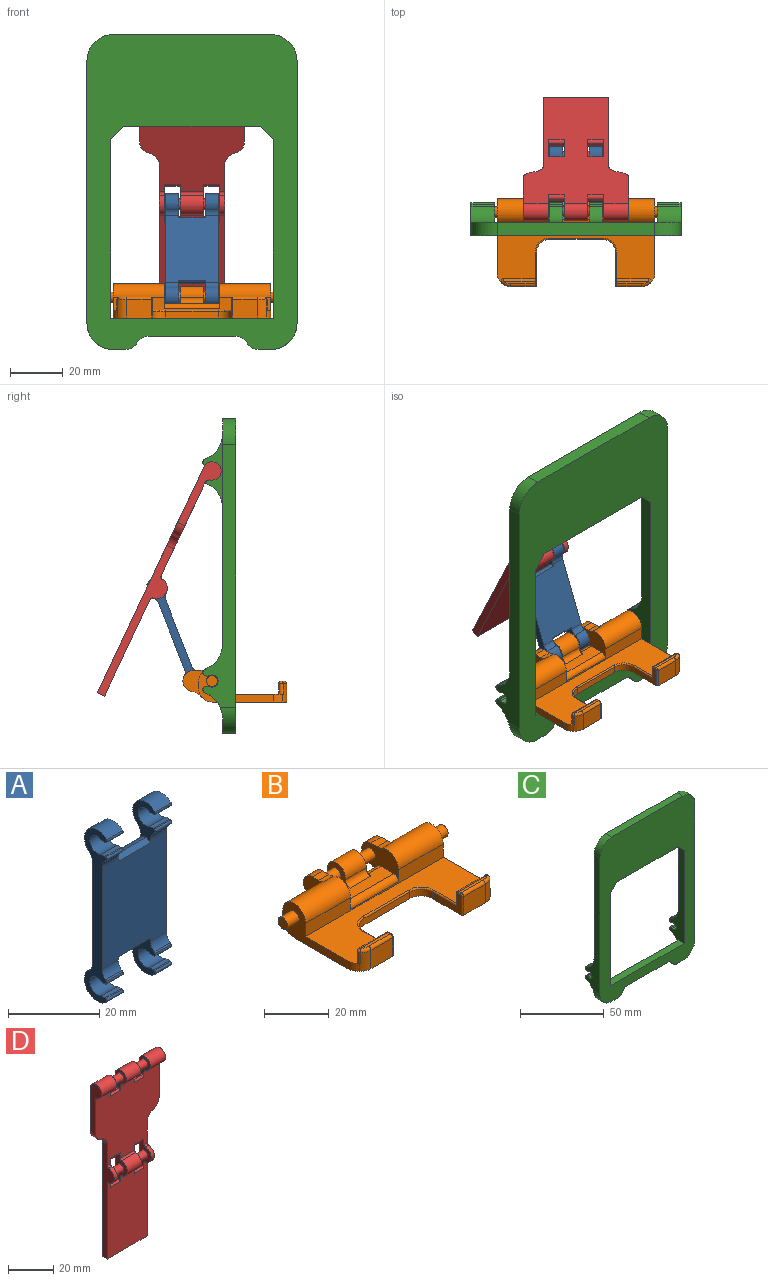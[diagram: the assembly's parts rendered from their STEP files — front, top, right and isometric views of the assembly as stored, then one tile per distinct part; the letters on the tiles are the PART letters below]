
ASSEMBLY  parts=4 mates=4
PART A: 56 faces, bbox 20x7x46 mm
  f0: cylinder r=3mm len=5mm, axis (-1,0,0), area 13.1mm2, adj f4,f7,f13,f17
  f1: cylinder r=3mm len=5mm, axis (-1,0,0), area 13.1mm2, adj f5,f7,f11,f16
  f2: cylinder r=3mm len=5mm, axis (-1,0,0), area 13.1mm2, adj f6,f10,f17,f19
  f3: cylinder r=3mm len=5mm, axis (-1,0,0), area 13.1mm2, adj f6,f12,f16,f18
  f4: cylinder r=4mm len=7.06mm, axis (-1,0,0), area 65mm2, adj f0,f7,f13,f41
  f5: cylinder r=4mm len=5mm, axis (-1,0,0), area 2.1mm2, adj f1,f7,f11,f44
  f6: plane 46x7.02mm, normal (1,0,0), area 144.3mm2, adj f2,f3,f8,f9,f16,f17,f18,f19
  f7: plane 46x7.02mm, normal (-1,0,0), area 144.3mm2, adj f0,f1,f4,f5,f14,f15,f16,f17
  f8: cylinder r=4mm len=7.06mm, axis (-1,0,0), area 65mm2, adj f6,f12,f42,f48
  f9: cylinder r=4mm len=5mm, axis (-1,0,0), area 2.1mm2, adj f6,f10,f46,f49
  f10: plane 10.2x7.02mm, normal (-1,0,0), area 32.3mm2, adj f2,f9,f16,f17,f19,f29,f30,f31
  f11: plane 10.2x7.02mm, normal (1,0,0), area 32.3mm2, adj f1,f5,f15,f16,f17,f26,f27,f28
  f12: plane 10.2x7.02mm, normal (-1,0,0), area 32.3mm2, adj f3,f8,f16,f17,f18,f23,f24,f25
  f13: plane 10.2x7.02mm, normal (1,0,0), area 32.3mm2, adj f0,f4,f14,f16,f17,f20,f21,f22
  f14: cylinder r=4mm len=5mm, axis (-1,0,0), area 2.1mm2, adj f7,f13,f40,f51
  f15: cylinder r=4mm len=7.06mm, axis (-1,0,0), area 65mm2, adj f7,f11,f45,f50
  f16: plane 27.28x20mm, normal (0,-1,0), area 528.8mm2, adj f1,f3,f6,f7,f10,f11,f12,f13
  f17: plane 27.28x20mm, normal (0,1,0), area 528.8mm2, adj f0,f2,f6,f7,f10,f11,f12,f13
  f18: cylinder r=4mm len=5mm, axis (-1,0,0), area 2.1mm2, adj f3,f6,f12,f43
  f19: cylinder r=4mm len=7.06mm, axis (-1,0,0), area 65mm2, adj f2,f6,f10,f47
  f20: plane 5x1.07mm, normal (0,0,1), area 5.4mm2, adj f7,f13,f22,f32
  f21: plane 5x1.07mm, normal (0,0,-1), area 5.4mm2, adj f7,f13,f22,f33
  f22: cylinder r=2.3mm len=5mm, axis (-1,0,0), area 49.9mm2, adj f7,f13,f20,f21
  f23: cylinder r=2.3mm len=5mm, axis (-1,0,0), area 49.9mm2, adj f6,f12,f24,f25
  f24: plane 5x1.07mm, normal (0,0,-1), area 5.4mm2, adj f6,f12,f23,f34
  f25: plane 5x1.07mm, normal (0,0,1), area 5.4mm2, adj f6,f12,f23,f35
  f26: plane 5x1.07mm, normal (0,0,1), area 5.4mm2, adj f7,f11,f28,f37
  f27: plane 5x1.07mm, normal (0,0,-1), area 5.4mm2, adj f7,f11,f28,f36
  f28: cylinder r=2.3mm len=5mm, axis (-1,0,0), area 49.9mm2, adj f7,f11,f26,f27
  f29: cylinder r=2.3mm len=5mm, axis (-1,0,0), area 49.9mm2, adj f6,f10,f30,f31
  f30: plane 5x1.07mm, normal (0,0,-1), area 5.4mm2, adj f6,f10,f29,f38
  f31: plane 5x1.07mm, normal (0,0,1), area 5.4mm2, adj f6,f10,f29,f39
  f32: cylinder r=1mm len=5mm, axis (-1,0,0), area 1.6mm2, adj f7,f13,f20,f40
  f33: cylinder r=1mm len=5mm, axis (-1,0,0), area 1.6mm2, adj f7,f13,f21,f41
  f34: cylinder r=1mm len=5mm, axis (-1,0,0), area 1.6mm2, adj f6,f12,f24,f42
  f35: cylinder r=1mm len=5mm, axis (-1,0,0), area 1.6mm2, adj f6,f12,f25,f43
  f36: cylinder r=1mm len=5mm, axis (-1,0,0), area 1.6mm2, adj f7,f11,f27,f44
  f37: cylinder r=1mm len=5mm, axis (-1,0,0), area 1.6mm2, adj f7,f11,f26,f45
  f38: cylinder r=1mm len=5mm, axis (-1,0,0), area 1.6mm2, adj f6,f10,f30,f46
  f39: cylinder r=1mm len=5mm, axis (-1,0,0), area 1.6mm2, adj f6,f10,f31,f47
  f40: cylinder r=0.5mm len=5mm, axis (-1,0,0), area 5mm2, adj f7,f13,f14,f32
  f41: cylinder r=0.5mm len=5mm, axis (1,0,0), area 5mm2, adj f4,f7,f13,f33
  f42: cylinder r=0.5mm len=5mm, axis (1,0,0), area 5mm2, adj f6,f8,f12,f34
  f43: cylinder r=0.5mm len=5mm, axis (-1,0,0), area 5mm2, adj f6,f12,f18,f35
  f44: cylinder r=0.5mm len=5mm, axis (1,0,0), area 5mm2, adj f5,f7,f11,f36
  f45: cylinder r=0.5mm len=5mm, axis (-1,0,0), area 5mm2, adj f7,f11,f15,f37
  f46: cylinder r=0.5mm len=5mm, axis (1,0,0), area 5mm2, adj f6,f9,f10,f38
  f47: cylinder r=0.5mm len=5mm, axis (-1,0,0), area 5mm2, adj f6,f10,f19,f39
  f48: cylinder r=3mm len=5mm, axis (-1,0,0), area 13.1mm2, adj f6,f8,f12,f17
  f49: cylinder r=3mm len=5mm, axis (-1,0,0), area 13.1mm2, adj f6,f9,f10,f16
  f50: cylinder r=3mm len=5mm, axis (-1,0,0), area 13.1mm2, adj f7,f11,f15,f17
  f51: cylinder r=3mm len=5mm, axis (-1,0,0), area 13.1mm2, adj f7,f13,f14,f16
  f52: cylinder r=2mm len=10mm, axis (-1,0,0), area 17.1mm2, adj f12,f13,f17,f53
  f53: cylinder r=2mm len=10mm, axis (1,0,0), area 17.1mm2, adj f12,f13,f16,f52
  f54: cylinder r=2mm len=10mm, axis (-1,0,0), area 17.1mm2, adj f10,f11,f16,f55
  f55: cylinder r=2mm len=10mm, axis (1,0,0), area 17.1mm2, adj f10,f11,f17,f54
PART B: 79 faces, bbox 70x39.9x13 mm
  f0: plane 60x22.15mm, normal (0,0,1), area 757.9mm2, adj f8,f9,f10,f43,f44,f46,f48,f50
  f1: plane 9.43x7mm, normal (0,-1,0), area 66mm2, adj f5,f50,f63,f78
  f2: cylinder r=2mm len=6mm, axis (-1,0,0), area 75.4mm2, adj f19,f28
  f3: cylinder r=5mm len=19.5mm, axis (-1,0,0), area 281.1mm2, adj f4,f8,f10,f14,f15,f42
  f4: plane 15x3mm, normal (0,1,0), area 45mm2, adj f3,f8,f14,f20
  f5: plane 60x28.4mm, normal (0,0,-1), area 1163.5mm2, adj f1,f7,f8,f9,f20,f34,f35,f36
  f6: plane 15x3mm, normal (0,1,0), area 45mm2, adj f9,f11,f18,f20
  f7: plane 9.43x7mm, normal (0,-1,0), area 66mm2, adj f5,f53,f59,f64
  f8: plane 28.33x13mm, normal (1,0,0), area 155mm2, adj f0,f3,f4,f5,f10,f20,f23,f52
  f9: plane 28.33x13mm, normal (-1,0,0), area 155mm2, adj f0,f5,f6,f10,f11,f20,f25,f51
  f10: plane 60x5mm, normal (0,-1,0), area 205.5mm2, adj f0,f3,f8,f9,f11,f15,f19,f45
  f11: cylinder r=5mm len=19.5mm, axis (-1,0,0), area 281.1mm2, adj f6,f9,f10,f18,f19,f41
  f12: plane 4.5x2.74mm, normal (0,0,1), area 12.3mm2, adj f13,f14,f15,f42
  f13: cylinder r=4mm len=7.96mm, axis (-1,0,0), area 53.9mm2, adj f12,f14,f15,f33
  f14: plane 10.63x8.92mm, normal (1,0,0), area 46mm2, adj f3,f4,f12,f13,f20,f33,f42
  f15: plane 16.1x11.13mm, normal (-1,0,0), area 100.1mm2, adj f3,f10,f12,f13,f20,f21,f26,f33
  f16: plane 4.5x2.74mm, normal (0,0,1), area 12.3mm2, adj f17,f18,f19,f41
  f17: cylinder r=4mm len=7.96mm, axis (1,0,0), area 53.9mm2, adj f16,f18,f19,f32
  f18: plane 10.63x8.92mm, normal (-1,0,0), area 46mm2, adj f6,f11,f16,f17,f20,f32,f41
  f19: plane 16.1x11.13mm, normal (1,0,0), area 100.1mm2, adj f2,f10,f11,f16,f17,f20,f21,f32
  f20: cylinder r=5mm len=60mm, axis (1,0,0), area 378.9mm2, adj f4,f5,f6,f8,f9,f14,f15,f18
  f21: plane 21x5.6mm, normal (0,0,1), area 104.3mm2, adj f15,f19,f27,f28,f30,f39,f40,f45
  f22: plane 4.2x4.2mm, normal (1,0,0), area 13.9mm2, adj f23
  f23: cylinder r=2.1mm len=5mm, axis (-1,0,0), area 66mm2, adj f8,f22
  f24: plane 4.2x4.2mm, normal (-1,0,0), area 13.9mm2, adj f25
  f25: cylinder r=2.1mm len=5mm, axis (1,0,0), area 66mm2, adj f9,f24
  f26: cylinder r=2mm len=6mm, axis (-1,0,0), area 75.4mm2, adj f15,f27
  f27: plane 10.13x9.98mm, normal (1,0,0), area 42.2mm2, adj f20,f21,f26,f29,f30,f31,f40
  f28: plane 10.13x9.98mm, normal (-1,0,0), area 42.2mm2, adj f2,f20,f21,f29,f30,f31,f39
  f29: cylinder r=4mm len=9mm, axis (-1,0,0), area 167.3mm2, adj f27,f28,f30,f31
  f30: cylinder r=2mm len=9mm, axis (-1,0,0), area 29.8mm2, adj f21,f27,f28,f29
  f31: cylinder r=6mm len=9mm, axis (-1,0,0), area 40.3mm2, adj f20,f27,f28,f29
  f32: cylinder r=6mm len=4.5mm, axis (1,0,0), area 20.1mm2, adj f17,f18,f19,f20
  f33: cylinder r=6mm len=4.5mm, axis (1,0,0), area 20.1mm2, adj f13,f14,f15,f20
  f34: plane 20x2.5mm, normal (0,-1,0), area 50mm2, adj f5,f37,f38,f71
  f35: plane 12.5x7.5mm, normal (1,0,0), area 41.1mm2, adj f5,f37,f73,f74,f75,f76,f77,f78
  f36: plane 12.5x7.5mm, normal (-1,0,0), area 41.1mm2, adj f5,f38,f64,f65,f66,f67,f68,f69
  f37: cylinder r=5mm len=5mm, axis (0,0,1), area 19.6mm2, adj f5,f34,f35,f72
  f38: cylinder r=5mm len=5mm, axis (0,0,-1), area 19.6mm2, adj f5,f34,f36,f70
  f39: cylinder r=2mm len=6mm, axis (1,0,0), area 25.1mm2, adj f19,f20,f21,f28
  f40: cylinder r=2mm len=6mm, axis (1,0,0), area 25.1mm2, adj f15,f20,f21,f27
  f41: cylinder r=5mm len=4.5mm, axis (-1,0,0), area 10.1mm2, adj f11,f16,f18,f19
  f42: cylinder r=5mm len=4.5mm, axis (-1,0,0), area 10.1mm2, adj f3,f12,f14,f15
  f43: plane 3x0.07mm, normal (0.71,-0.71,0), area 0.3mm2, adj f0,f5,f52,f53
  f44: plane 3x0.07mm, normal (-0.71,-0.71,0), area 0.3mm2, adj f0,f5,f50,f51
  f45: cylinder r=2mm len=21mm, axis (-1,0,0), area 66mm2, adj f10,f15,f19,f21
  f46: plane 12.07x4mm, normal (0,1,0), area 48.3mm2, adj f0,f55,f60,f74
  f47: plane 12.07x1mm, normal (0,0,1), area 11.2mm2, adj f55,f62,f63,f76
  f48: plane 12.07x4mm, normal (0,1,0), area 48.3mm2, adj f0,f54,f56,f68
  f49: plane 12.07x1mm, normal (0,0,1), area 11.2mm2, adj f54,f58,f59,f66
  f50: cylinder r=5mm len=7mm, axis (0,0,-1), area 26.2mm2, adj f0,f1,f5,f44,f60,f62
  f51: cylinder r=5mm len=3.54mm, axis (0,0,-1), area 11.8mm2, adj f0,f5,f9,f44
  f52: cylinder r=5mm len=3.54mm, axis (0,0,1), area 11.8mm2, adj f0,f5,f8,f43
  f53: cylinder r=5mm len=7mm, axis (0,0,-1), area 26.2mm2, adj f0,f5,f7,f43,f56,f58
  f54: cylinder r=1mm len=12.07mm, axis (1,0,0), area 19mm2, adj f48,f49,f57,f67
  f55: cylinder r=1mm len=12.07mm, axis (1,0,0), area 19mm2, adj f46,f47,f61,f75
  f56: cylinder r=1mm len=4mm, axis (0,0,-1), area 9.7mm2, adj f0,f48,f53,f57
  f57: sphere r=1mm, area 2.4mm2, adj f54,f56,f58
  f58: torus R=4mm, axis (0,0,1), area 5.3mm2, adj f49,f53,f57,f59
  f59: cylinder r=1mm len=9.43mm, axis (-1,0,0), area 14.8mm2, adj f7,f49,f58,f65
  f60: cylinder r=1mm len=4mm, axis (0,0,-1), area 9.7mm2, adj f0,f46,f50,f61
  f61: sphere r=1mm, area 2.4mm2, adj f55,f60,f62
  f62: torus R=4mm, axis (0,0,1), area 5.3mm2, adj f47,f50,f61,f63
  f63: cylinder r=1mm len=9.43mm, axis (-1,0,0), area 14.8mm2, adj f1,f47,f62,f77
  f64: cylinder r=0.5mm len=7mm, axis (0,0,1), area 5.5mm2, adj f5,f7,f36,f65
  f65: torus R=0.5mm, axis (-1,0,0), area 1mm2, adj f36,f59,f64,f66
  f66: cylinder r=0.5mm len=1mm, axis (0,-1,0), area 0.8mm2, adj f36,f49,f65,f67
  f67: torus R=0.5mm, axis (-1,0,0), area 1mm2, adj f36,f54,f66,f68
  f68: cylinder r=0.5mm len=4.5mm, axis (0,0,-1), area 3.3mm2, adj f36,f48,f67,f69
  f69: cylinder r=0.5mm len=10.5mm, axis (0,1,0), area 8mm2, adj f0,f36,f68,f70
  f70: torus R=5.5mm, axis (0,0,-1), area 6.4mm2, adj f0,f38,f69,f71
  f71: cylinder r=0.5mm len=20mm, axis (-1,0,0), area 15.7mm2, adj f0,f34,f70,f72
  f72: torus R=5.5mm, axis (0,0,-1), area 6.4mm2, adj f0,f37,f71,f73
  f73: cylinder r=0.5mm len=10.5mm, axis (0,-1,0), area 8mm2, adj f0,f35,f72,f74
  f74: cylinder r=0.5mm len=4.5mm, axis (0,0,-1), area 3.3mm2, adj f35,f46,f73,f75
  f75: torus R=0.5mm, axis (-1,0,0), area 1mm2, adj f35,f55,f74,f76
  f76: cylinder r=0.5mm len=1mm, axis (0,1,0), area 0.8mm2, adj f35,f47,f75,f77
  f77: torus R=0.5mm, axis (-1,0,0), area 1mm2, adj f35,f63,f76,f78
  f78: cylinder r=0.5mm len=7mm, axis (0,0,-1), area 5.5mm2, adj f1,f5,f35,f77
PART C: 79 faces, bbox 80x12.5x120 mm
  f0: plane 78.31x11.9mm, normal (0,1,0), area 594.8mm2, adj f3,f6,f9,f10,f12,f13,f14,f15
  f1: plane 120x80mm, normal (0,-1,0), area 4797.1mm2, adj f3,f4,f5,f6,f7,f8,f9,f10
  f2: plane 85.98x80mm, normal (0,1,0), area 3419.3mm2, adj f4,f5,f7,f8,f11,f17,f18,f24
  f3: plane 5x4.68mm, normal (0,0,-1), area 23.4mm2, adj f0,f1,f9,f16
  f4: plane 60x5mm, normal (0,0,1), area 300mm2, adj f1,f2,f8,f11
  f5: plane 100x12.49mm, normal (-1,0,0), area 577.9mm2, adj f1,f2,f8,f9,f38,f39,f40,f41
  f6: plane 5x4.68mm, normal (0,0,-1), area 23.4mm2, adj f0,f1,f10,f15
  f7: plane 100x12.49mm, normal (1,0,0), area 577.9mm2, adj f1,f2,f10,f11,f25,f26,f27,f28
  f8: cylinder r=10mm len=10mm, axis (0,1,0), area 78.5mm2, adj f1,f2,f4,f5
  f9: cylinder r=10mm len=10mm, axis (0,-1,0), area 79.7mm2, adj f0,f1,f3,f5,f60
  f10: cylinder r=10mm len=10mm, axis (0,1,0), area 79.7mm2, adj f0,f1,f6,f7,f63
  f11: cylinder r=10mm len=10mm, axis (0,-1,0), area 78.5mm2, adj f1,f2,f4,f7
  f12: plane 33.32x5mm, normal (0,0,-1), area 166.6mm2, adj f0,f1,f13,f14
  f13: cylinder r=5mm len=5mm, axis (0,1,0), area 26.2mm2, adj f0,f1,f12,f16
  f14: cylinder r=5mm len=5mm, axis (0,-1,0), area 26.2mm2, adj f0,f1,f12,f15
  f15: cylinder r=5mm len=5mm, axis (0,-1,0), area 26.2mm2, adj f0,f1,f6,f14
  f16: cylinder r=5mm len=5mm, axis (0,1,0), area 26.2mm2, adj f0,f1,f3,f13
  f17: plane 28.04x7.49mm, normal (1,0,0), area 79mm2, adj f2,f19,f20,f21,f22,f23,f51,f52
  f18: plane 28.04x7.49mm, normal (-1,0,0), area 79mm2, adj f2,f19,f20,f21,f22,f23,f51,f52
  f19: cylinder r=5.25mm len=5mm, axis (-1,0,0), area 4.5mm2, adj f17,f18,f54,f65
  f20: plane 5x0.31mm, normal (0,0,1), area 1.5mm2, adj f17,f18,f53,f75
  f21: cylinder r=2.3mm len=5mm, axis (-1,0,0), area 46.1mm2, adj f17,f18,f75,f76
  f22: plane 5x0.31mm, normal (0,0,-1), area 1.5mm2, adj f17,f18,f52,f76
  f23: cylinder r=5.25mm len=5mm, axis (-1,0,0), area 4.5mm2, adj f17,f18,f51,f66
  f24: plane 74.02x12.49mm, normal (-1,0,0), area 419.5mm2, adj f0,f1,f2,f25,f26,f27,f28,f29
  f25: cylinder r=5.25mm len=9mm, axis (-1,0,0), area 8mm2, adj f7,f24,f46,f63
  f26: plane 9x0.31mm, normal (0,0,1), area 2.8mm2, adj f7,f24,f45,f74
  f27: cylinder r=2.3mm len=9mm, axis (-1,0,0), area 83mm2, adj f7,f24,f73,f74
  f28: plane 9x0.31mm, normal (0,0,-1), area 2.8mm2, adj f7,f24,f44,f73
  f29: cylinder r=5.25mm len=9mm, axis (-1,0,0), area 8mm2, adj f7,f24,f43,f64
  f30: plane 28.04x7.49mm, normal (-1,0,0), area 79mm2, adj f2,f32,f33,f34,f35,f36,f55,f56
  f31: plane 28.04x7.49mm, normal (1,0,0), area 79mm2, adj f2,f32,f33,f34,f35,f36,f55,f56
  f32: cylinder r=5.25mm len=5mm, axis (1,0,0), area 4.5mm2, adj f30,f31,f56,f61
  f33: plane 5x0.31mm, normal (0,0,-1), area 1.5mm2, adj f30,f31,f55,f72
  f34: cylinder r=2.3mm len=5mm, axis (1,0,0), area 46.1mm2, adj f30,f31,f71,f72
  f35: plane 5x0.31mm, normal (0,0,1), area 1.5mm2, adj f30,f31,f58,f71
  f36: cylinder r=5.25mm len=5mm, axis (1,0,0), area 4.5mm2, adj f30,f31,f57,f62
  f37: plane 74.02x12.49mm, normal (1,0,0), area 419.5mm2, adj f0,f1,f2,f38,f39,f40,f41,f42
  f38: cylinder r=5.25mm len=9mm, axis (1,0,0), area 8mm2, adj f5,f37,f48,f59
  f39: plane 9x0.31mm, normal (0,0,-1), area 2.8mm2, adj f5,f37,f47,f69
  f40: cylinder r=2.3mm len=9mm, axis (1,0,0), area 83mm2, adj f5,f37,f69,f70
  f41: plane 9x0.31mm, normal (0,0,1), area 2.8mm2, adj f5,f37,f50,f70
  f42: cylinder r=5.25mm len=9mm, axis (1,0,0), area 8mm2, adj f5,f37,f49,f60
  f43: cylinder r=1.4mm len=9mm, axis (-1,0,0), area 17.3mm2, adj f7,f24,f29,f44
  f44: cylinder r=1.4mm len=9mm, axis (-1,0,0), area 14.4mm2, adj f7,f24,f28,f43
  f45: cylinder r=1.4mm len=9mm, axis (-1,0,0), area 14.4mm2, adj f7,f24,f26,f46
  f46: cylinder r=1.4mm len=9mm, axis (-1,0,0), area 17.3mm2, adj f7,f24,f25,f45
  f47: cylinder r=1.4mm len=9mm, axis (1,0,0), area 14.4mm2, adj f5,f37,f39,f48
  f48: cylinder r=1.4mm len=9mm, axis (1,0,0), area 17.3mm2, adj f5,f37,f38,f47
  f49: cylinder r=1.4mm len=9mm, axis (1,0,0), area 17.3mm2, adj f5,f37,f42,f50
  f50: cylinder r=1.4mm len=9mm, axis (1,0,0), area 14.4mm2, adj f5,f37,f41,f49
  f51: cylinder r=1.4mm len=5mm, axis (-1,0,0), area 9.6mm2, adj f17,f18,f23,f52
  f52: cylinder r=1.4mm len=5mm, axis (1,0,0), area 8mm2, adj f17,f18,f22,f51
  f53: cylinder r=1.4mm len=5mm, axis (-1,0,0), area 8mm2, adj f17,f18,f20,f54
  f54: cylinder r=1.4mm len=5mm, axis (-1,0,0), area 9.6mm2, adj f17,f18,f19,f53
  f55: cylinder r=1.4mm len=5mm, axis (-1,0,0), area 8mm2, adj f30,f31,f33,f56
  f56: cylinder r=1.4mm len=5mm, axis (1,0,0), area 9.6mm2, adj f30,f31,f32,f55
  f57: cylinder r=1.4mm len=5mm, axis (1,0,0), area 9.6mm2, adj f30,f31,f36,f58
  f58: cylinder r=1.4mm len=5mm, axis (1,0,0), area 8mm2, adj f30,f31,f35,f57
  f59: cylinder r=10mm len=9.19mm, axis (1,0,0), area 105mm2, adj f2,f5,f37,f38
  f60: cylinder r=10mm len=9.19mm, axis (1,0,0), area 103.9mm2, adj f0,f5,f9,f37,f42
  f61: cylinder r=10mm len=9.19mm, axis (1,0,0), area 58.3mm2, adj f2,f30,f31,f32
  f62: cylinder r=10mm len=9.19mm, axis (1,0,0), area 58.3mm2, adj f2,f30,f31,f36
  f63: cylinder r=10mm len=9.19mm, axis (-1,0,0), area 103.9mm2, adj f0,f7,f10,f24,f25
  f64: cylinder r=10mm len=9.19mm, axis (-1,0,0), area 105mm2, adj f2,f7,f24,f29
  f65: cylinder r=10mm len=9.19mm, axis (-1,0,0), area 58.3mm2, adj f2,f17,f18,f19
  f66: cylinder r=10mm len=9.19mm, axis (-1,0,0), area 58.3mm2, adj f2,f17,f18,f23
  f67: plane 52x5mm, normal (0,0,-1), area 260mm2, adj f1,f2,f77,f78
  f68: plane 62x5mm, normal (0,0,1), area 310mm2, adj f0,f1,f24,f37
  f69: cylinder r=2mm len=9mm, axis (1,0,0), area 7.8mm2, adj f5,f37,f39,f40
  f70: cylinder r=2mm len=9mm, axis (1,0,0), area 7.8mm2, adj f5,f37,f40,f41
  f71: cylinder r=2mm len=5mm, axis (1,0,0), area 4.3mm2, adj f30,f31,f34,f35
  f72: cylinder r=2mm len=5mm, axis (1,0,0), area 4.3mm2, adj f30,f31,f33,f34
  f73: cylinder r=2mm len=9mm, axis (-1,0,0), area 7.8mm2, adj f7,f24,f27,f28
  f74: cylinder r=2mm len=9mm, axis (-1,0,0), area 7.8mm2, adj f7,f24,f26,f27
  f75: cylinder r=2mm len=5mm, axis (-1,0,0), area 4.3mm2, adj f17,f18,f20,f21
  f76: cylinder r=2mm len=5mm, axis (-1,0,0), area 4.3mm2, adj f17,f18,f21,f22
  f77: plane 5x5mm, normal (-0.71,0,-0.71), area 35.4mm2, adj f1,f2,f24,f67
  f78: plane 5x5mm, normal (0.71,0,-0.71), area 35.4mm2, adj f1,f2,f37,f67
PART D: 57 faces, bbox 40x7.5x98.5 mm
  f0: cylinder r=4mm len=9mm, axis (-1,0,0), area 105.9mm2, adj f1,f2,f33,f40
  f1: cylinder r=1mm len=9mm, axis (-1,0,0), area 13.2mm2, adj f0,f12,f33,f40
  f2: cylinder r=1mm len=9mm, axis (-1,0,0), area 13.2mm2, adj f0,f9,f33,f40
  f3: plane 95x40mm, normal (0,1,0), area 2523.8mm2, adj f5,f11,f13,f14,f15,f16,f17,f18
  f4: cylinder r=2mm len=9mm, axis (-1,0,0), area 23.3mm2, adj f9,f11,f29,f36
  f5: cylinder r=3.5mm len=9.5mm, axis (-1,0,0), area 147.5mm2, adj f3,f14,f24,f35
  f6: cylinder r=4mm len=7.96mm, axis (-1,0,0), area 23.5mm2, adj f7,f8,f16,f39
  f7: cylinder r=1mm len=2mm, axis (-1,0,0), area 2.9mm2, adj f6,f12,f16,f39
  f8: cylinder r=1mm len=2mm, axis (-1,0,0), area 2.9mm2, adj f6,f9,f16,f39
  f9: plane 40x39.08mm, normal (0,-1,0), area 1254.7mm2, adj f2,f4,f8,f10,f14,f15,f16,f17
  f10: cylinder r=2mm len=9.5mm, axis (-1,0,0), area 24.6mm2, adj f9,f15,f22,f28
  f11: cylinder r=3.5mm len=9mm, axis (-1,0,0), area 139.7mm2, adj f3,f4,f29,f36
  f12: plane 40.68x25mm, normal (0,-1,0), area 982.3mm2, adj f1,f7,f13,f16,f18,f25,f32,f33
  f13: plane 25x3mm, normal (0,0,-1), area 75mm2, adj f3,f12,f16,f18
  f14: plane 26.82x7mm, normal (-1,0,0), area 101.1mm2, adj f3,f5,f9,f21,f24
  f15: plane 26.82x7mm, normal (1,0,0), area 101.1mm2, adj f3,f9,f10,f20,f22
  f16: plane 62x7.5mm, normal (-1,0,0), area 215.5mm2, adj f3,f6,f7,f8,f9,f12,f13,f17
  f17: cylinder r=5mm len=4.84mm, axis (0,1,0), area 19.8mm2, adj f3,f9,f16,f21
  f18: plane 62x7.5mm, normal (1,0,0), area 215.5mm2, adj f3,f9,f12,f13,f19,f23,f25,f26
  f19: cylinder r=5mm len=4.84mm, axis (0,1,0), area 19.8mm2, adj f3,f9,f18,f20
  f20: cylinder r=5mm len=4.84mm, axis (0,1,0), area 19.8mm2, adj f3,f9,f15,f19
  f21: cylinder r=5mm len=4.84mm, axis (0,1,0), area 19.8mm2, adj f3,f9,f14,f17
  f22: cylinder r=3.5mm len=9.5mm, axis (-1,0,0), area 147.5mm2, adj f3,f10,f15,f28
  f23: cylinder r=4mm len=7.96mm, axis (-1,0,0), area 23.5mm2, adj f18,f25,f26,f32
  f24: cylinder r=2mm len=9.5mm, axis (-1,0,0), area 24.6mm2, adj f5,f9,f14,f35
  f25: cylinder r=1mm len=2mm, axis (-1,0,0), area 2.9mm2, adj f12,f18,f23,f32
  f26: cylinder r=1mm len=2mm, axis (-1,0,0), area 2.9mm2, adj f9,f18,f23,f32
  f27: cylinder r=7mm len=6mm, axis (-1,0,0), area 5.4mm2, adj f28,f29,f55,f56
  f28: plane 11.36x7mm, normal (-1,0,0), area 39.2mm2, adj f3,f9,f10,f22,f27,f42,f55,f56
  f29: plane 11.36x7mm, normal (1,0,0), area 39.2mm2, adj f3,f4,f9,f11,f27,f42,f55,f56
  f30: cylinder r=7mm len=6mm, axis (-1,0,0), area 5.4mm2, adj f32,f33,f51,f53
  f31: cylinder r=7mm len=6mm, axis (-1,0,0), area 5.4mm2, adj f32,f33,f52,f54
  f32: plane 15.72x7.5mm, normal (-1,0,0), area 58.1mm2, adj f3,f9,f12,f23,f25,f26,f30,f31
  f33: plane 15.72x7.5mm, normal (1,0,0), area 58.1mm2, adj f0,f1,f2,f3,f9,f12,f30,f31
  f34: cylinder r=7mm len=6mm, axis (1,0,0), area 5.4mm2, adj f35,f36,f49,f50
  f35: plane 11.36x7mm, normal (1,0,0), area 39.2mm2, adj f3,f5,f9,f24,f34,f41,f49,f50
  f36: plane 11.36x7mm, normal (-1,0,0), area 39.2mm2, adj f3,f4,f9,f11,f34,f41,f49,f50
  f37: cylinder r=7mm len=6mm, axis (1,0,0), area 5.4mm2, adj f39,f40,f45,f47
  f38: cylinder r=7mm len=6mm, axis (1,0,0), area 5.4mm2, adj f39,f40,f46,f48
  f39: plane 15.72x7.5mm, normal (1,0,0), area 58.1mm2, adj f3,f6,f7,f8,f9,f12,f37,f38
  f40: plane 15.72x7.5mm, normal (-1,0,0), area 58.1mm2, adj f0,f1,f2,f3,f9,f12,f37,f38
  f41: cylinder r=2mm len=6mm, axis (-1,0,0), area 75.4mm2, adj f35,f36
  f42: cylinder r=2mm len=6mm, axis (-1,0,0), area 75.4mm2, adj f28,f29
  f43: cylinder r=2mm len=6mm, axis (-1,0,0), area 75.4mm2, adj f39,f40
  f44: cylinder r=2mm len=6mm, axis (-1,0,0), area 75.4mm2, adj f32,f33
  f45: cylinder r=1mm len=6mm, axis (1,0,0), area 8.3mm2, adj f9,f37,f39,f40
  f46: cylinder r=1mm len=6mm, axis (1,0,0), area 8.3mm2, adj f12,f38,f39,f40
  f47: cylinder r=1mm len=6mm, axis (1,0,0), area 11.3mm2, adj f3,f37,f39,f40
  f48: cylinder r=1mm len=6mm, axis (1,0,0), area 11.3mm2, adj f3,f38,f39,f40
  f49: cylinder r=1mm len=6mm, axis (1,0,0), area 8.3mm2, adj f9,f34,f35,f36
  f50: cylinder r=1mm len=6mm, axis (1,0,0), area 11.3mm2, adj f3,f34,f35,f36
  f51: cylinder r=1mm len=6mm, axis (-1,0,0), area 8.3mm2, adj f9,f30,f32,f33
  f52: cylinder r=1mm len=6mm, axis (-1,0,0), area 8.3mm2, adj f12,f31,f32,f33
  f53: cylinder r=1mm len=6mm, axis (-1,0,0), area 11.3mm2, adj f3,f30,f32,f33
  f54: cylinder r=1mm len=6mm, axis (-1,0,0), area 11.3mm2, adj f3,f31,f32,f33
  f55: cylinder r=1mm len=6mm, axis (-1,0,0), area 8.3mm2, adj f9,f27,f28,f29
  f56: cylinder r=1mm len=6mm, axis (-1,0,0), area 11.3mm2, adj f3,f27,f28,f29
PLACE A rot(axis=(1,0,0),158.5deg) t=(0,23.06,25.78)mm
PLACE B rot(axis=(-1,0.05,0.07),0deg) t=(0,9.1,0.1)mm
PLACE C t=(0,0,8.1)mm
PLACE D rot(axis=(1,0,0),25.2deg) t=(0,12.17,89.59)mm
MATE revolute D.f41 <-> C.f19  axis (-1,0,0) through (7.5,9,88.1)mm
MATE revolute B.f2 <-> A.f22  axis (-1,0,0) through (7.5,16.1,8.1)mm
MATE revolute A.f28 <-> D.f0  axis (-1,0,0) through (7.5,30.03,43.45)mm
MATE revolute B.f3 <-> C.f25  axis (1,0,0) through (30,9,8.1)mm
